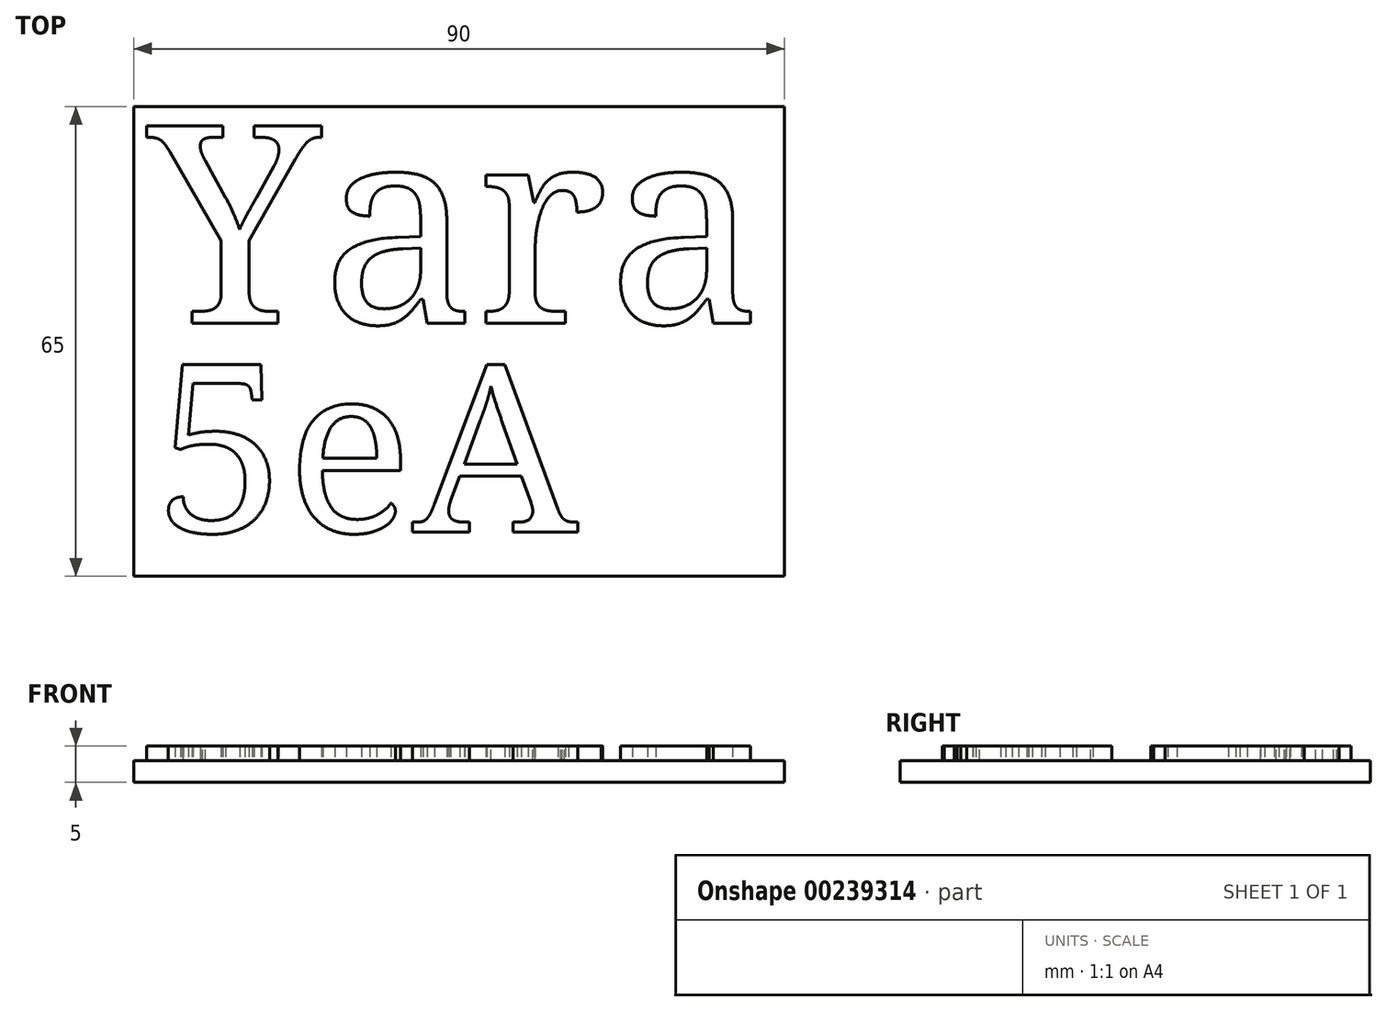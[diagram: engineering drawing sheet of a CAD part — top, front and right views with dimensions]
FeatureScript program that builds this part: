
annotation { "Feature Type Name" : "Feature", "Feature Type Description" : "" }
export const myFeature = defineFeature(function(context is Context, id is Id, definition is map)
    precondition{}
    {
        {
            var Q0;
            Q0=qCreatedBy(makeId("Top.planeOp"),FACE);
            var sketch = newSketch(context, id + "F0", { "sketchPlane" : qUnion([Q0])});
            skLineSegment(sketch, "E0.bottom", {"start": v(0, 0) * mm, "end": v(90, 0) * mm});
            skLineSegment(sketch, "E0.top", {"start": v(0, -65) * mm, "end": v(90, -65) * mm});
            skLineSegment(sketch, "E0.left", {"start": v(0, 0) * mm, "end": v(0, -65) * mm});
            skLineSegment(sketch, "E0.right", {"start": v(90, 0) * mm, "end": v(90, -65) * mm});
            skSolve(sketch);
        }
        {
            var Q0;
            Q0=makeQuery(id+"F0.imprint","IMPRINT",FACE,{"disambiguationData":[TD([[makeQuery(id+"F0.imprint","IMPRINT",EDGE,{"derivedFrom":sQuery(id+"F0.wireOp",EDGE,"E0.bottom")}),-1.0]])]});
            extrude(context, id + "F1", {"entities" : qUnion([Q0]), "depth" : 3 * mm});
        }
        {
            var Q0;
            Q0=makeQuery(id+"F1.opExtrude","CAP_FACE",FACE,{"disambiguationData":[OSD([sQuery(id+"F0.wireOp",EDGE,"E0.bottom"),sQuery(id+"F0.wireOp",EDGE,"E0.top"),sQuery(id+"F0.wireOp",EDGE,"E0.left"),sQuery(id+"F0.wireOp",EDGE,"E0.right")])],"isStart":false});
            var sketch = newSketch(context, id + "F2", { "sketchPlane" : qUnion([Q0])});
            skText(sketch, "E1", { "text": "Yara\n\n", "fontName": "NotoSerif-Regular.ttf"});
            skText(sketch, "E2", { "text": "5eA", "fontName": "NotoSerif-Regular.ttf"});
            const initialGuessF2  = {"E1": [0.002, -0.02997, 1, 0, 0.02753], "E2": [0.00302, -0.05887, 1, 0, 0.02337]};
            skSetInitialGuess(sketch, initialGuessF2);
            skSolve(sketch);
        }
        {
            var Q0;
            Q0 = qSketchRegion(id + "F2", true);
            extrude(context, id + "F3", {"entities" : qUnion([Q0]), "operationType" : NewBodyOperationType.ADD, "depth" : 2 * mm});
        }
    });
